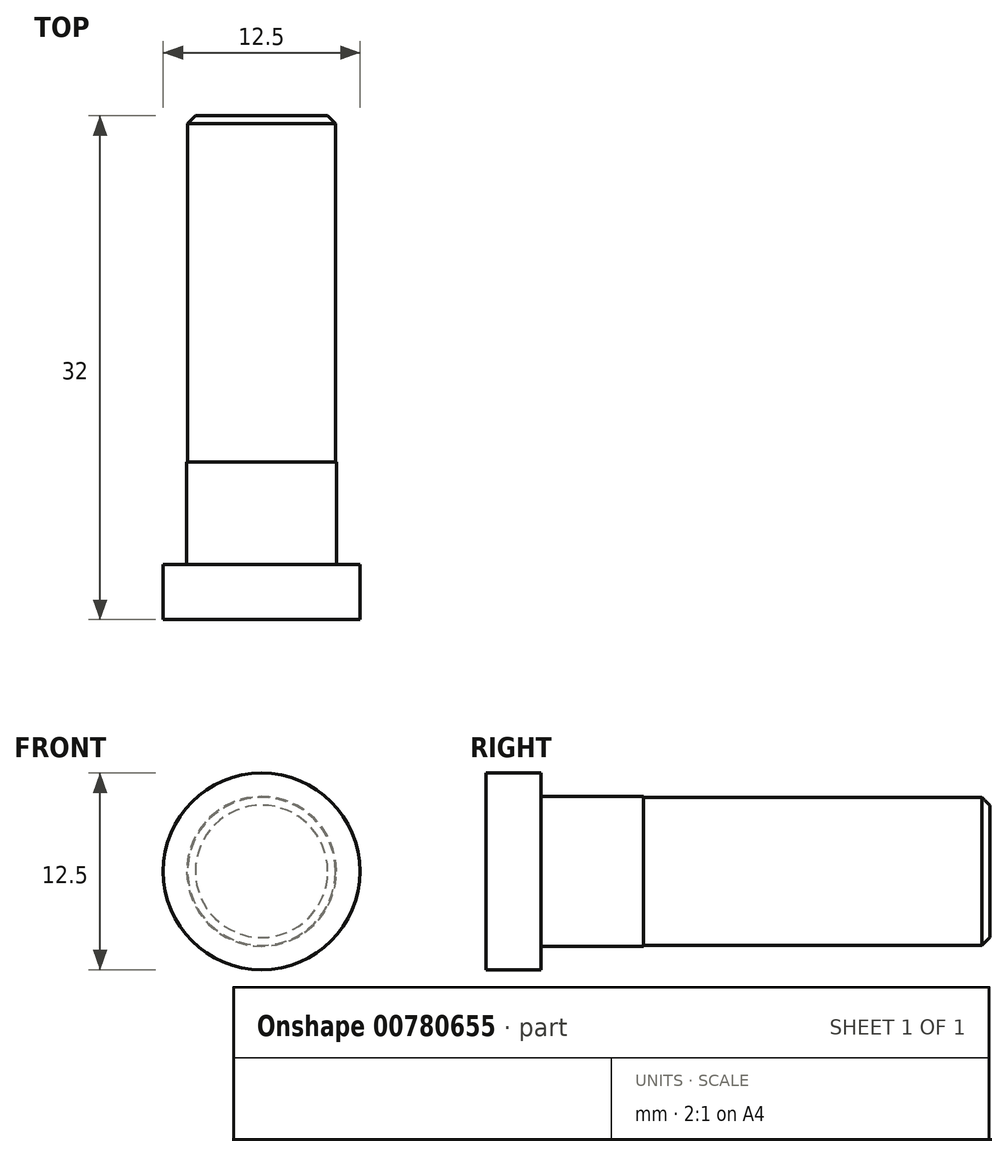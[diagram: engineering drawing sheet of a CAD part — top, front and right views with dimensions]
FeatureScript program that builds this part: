
annotation { "Feature Type Name" : "Feature", "Feature Type Description" : "" }
export const myFeature = defineFeature(function(context is Context, id is Id, definition is map)
    precondition{}
    {
        {
            var Q0;
            Q0=qCreatedBy(makeId("Front.planeOp"),FACE);
            var sketch = newSketch(context, id + "F0", { "sketchPlane" : qUnion([Q0])});
            skCircle(sketch, "E0", {"center": v(0, 0) * mm, "radius": 6.25 * mm});
            skSolve(sketch);
        }
        {
            var Q0;
            Q0 = qSketchRegion(id + "F0", true);
            extrude(context, id + "F1", {"entities" : qUnion([Q0]), "oppositeDirection" : true, "depth" : 3.5 * mm, "offsetDistance" : 25 * mm});
        }
        {
            var Q0;
            Q0=makeQuery(id+"F1.opExtrude","CAP_FACE",FACE,{"disambiguationData":[OSD([sQuery(id+"F0.wireOp",EDGE,"E0")])],"isStart":false});
            var sketch = newSketch(context, id + "F2", { "sketchPlane" : qUnion([Q0])});
            skCircle(sketch, "E1", {"center": v(0, 0) * mm, "radius": 4.75 * mm});
            skSolve(sketch);
        }
        {
            var Q0;
            Q0 = qSketchRegion(id + "F2", true);
            extrude(context, id + "F3", {"entities" : qUnion([Q0]), "operationType" : NewBodyOperationType.ADD, "depth" : 6.5 * mm, "offsetDistance" : 25 * mm});
        }
        {
            var Q0;
            Q0=makeQuery(id+"F3.opExtrude","CAP_FACE",FACE,{"disambiguationData":[OSD([sQuery(id+"F2.wireOp",EDGE,"E1")])],"isStart":false});
            var sketch = newSketch(context, id + "F4", { "sketchPlane" : qUnion([Q0])});
            skCircle(sketch, "E2", {"center": v(0, 0) * mm, "radius": 4.7 * mm});
            skSolve(sketch);
        }
        {
            var Q0;
            Q0 = qSketchRegion(id + "F4", true);
            extrude(context, id + "F5", {"entities" : qUnion([Q0]), "operationType" : NewBodyOperationType.ADD, "depth" : 22 * mm, "offsetDistance" : 25 * mm});
        }
        {
            var Q0;
            Q0=makeQuery(id+"F5.opExtrude","CAP_EDGE",EDGE,{"disambiguationData":[OSD([sQuery(id+"F4.wireOp",EDGE,"E2")])],"isStart":false});
            chamfer(context, id + "F6", {"entities" : qUnion([Q0]), "width" : 0.5 * mm, "tangentPropagation" : true});
        }
    });
